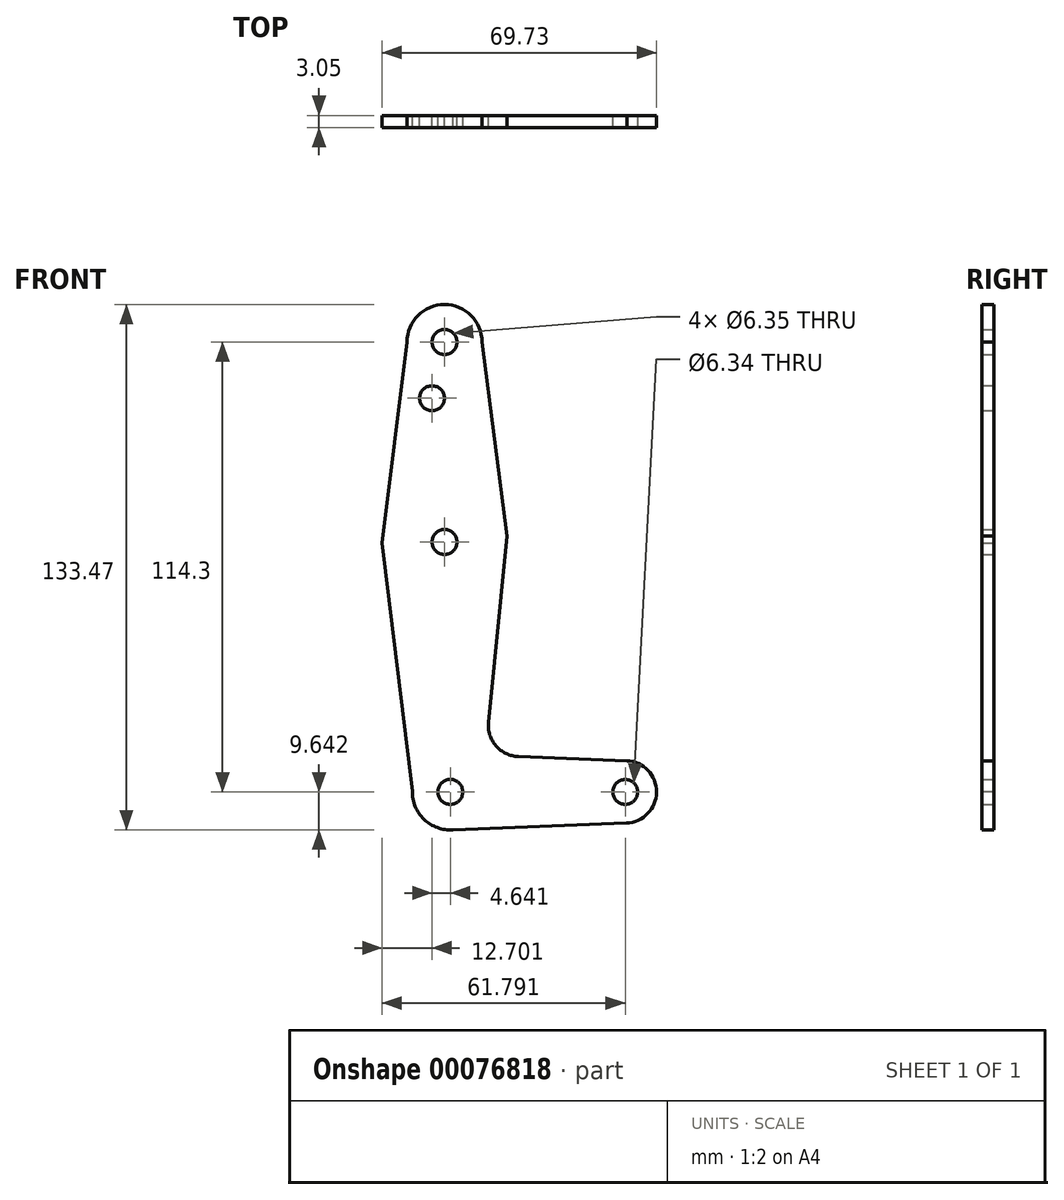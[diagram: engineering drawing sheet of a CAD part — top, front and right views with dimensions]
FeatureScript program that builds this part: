
annotation { "Feature Type Name" : "Feature", "Feature Type Description" : "" }
export const myFeature = defineFeature(function(context is Context, id is Id, definition is map)
    precondition{}
    {
        {
            var Q0;
            Q0=qCreatedBy(makeId("Front.planeOp"),FACE);
            var sketch = newSketch(context, id + "F0", { "sketchPlane" : qUnion([Q0])});
            skLineSegment(sketch, "E0", {"start": v(-40.14, -49.22) * mm, "end": v(4.31, -49.22) * mm});
            skCircle(sketch, "E1", {"center": v(-41.6, 65.08) * mm, "radius": 9.53 * mm});
            skCircle(sketch, "E2", {"center": v(-41.6, 14.28) * mm, "radius": 15.88 * mm});
            skCircle(sketch, "E3", {"center": v(-40.14, -49.22) * mm, "radius": 9.65 * mm});
            skCircle(sketch, "E4", {"center": v(4.31, -49.22) * mm, "radius": 7.94 * mm});
            skLineSegment(sketch, "E5", {"start": v(-41.6, 65.08) * mm, "end": v(-41.6, 14.28) * mm});
            skLineSegment(sketch, "E6", {"start": v(-41.6, 14.28) * mm, "end": v(-40.14, -49.22) * mm});
            skLineSegment(sketch, "E7", {"start": v(-32.08, 65.08) * mm, "end": v(-25.8, 15.75) * mm});
            skLineSegment(sketch, "E8", {"start": v(-25.8, 15.75) * mm, "end": v(-30.45, -31.5) * mm});
            skLineSegment(sketch, "E9", {"start": v(-49.78, -49.04) * mm, "end": v(-57.48, 14) * mm});
            skLineSegment(sketch, "E10", {"start": v(-51.13, 65.08) * mm, "end": v(-57.48, 14) * mm});
            skLineSegment(sketch, "E11", {"start": v(4.7, -41.29) * mm, "end": v(-22.85, -40.23) * mm});
            skLineSegment(sketch, "E12", {"start": v(-39.48, -58.84) * mm, "end": v(4.62, -57.15) * mm});
            skCircle(sketch, "E13", {"center": v(-41.6, 65.08) * mm, "radius": 3.18 * mm});
            skCircle(sketch, "E14", {"center": v(-41.6, 14.28) * mm, "radius": 3.18 * mm});
            skCircle(sketch, "E15", {"center": v(-40.14, -49.22) * mm, "radius": 3.18 * mm});
            skCircle(sketch, "E16", {"center": v(4.31, -49.22) * mm, "radius": 3.17 * mm});
            skArc(sketch, "E17.filletArc", {"start": v(-30.45, -31.5) * mm, "mid": v(-28.53, -37.51) * mm, "end": v(-22.85, -40.23) * mm});
            skCircle(sketch, "E18", {"center": v(-44.78, 50.8) * mm, "radius": 3.18 * mm});
            skSolve(sketch);
        }
        {
            var Q0;
            {var subQ0=sQuery(id+"F0.wireOp",EDGE,"E18");Q0=makeQuery(id+"F0.imprint","IMPRINT",FACE,{"disambiguationData":[TD([[makeQuery(id+"F0.imprint","IMPRINT",EDGE,{"derivedFrom":subQ0}),-1.0]])]});}
            var Q1;
            {var subQ4=sQuery(id+"F0.wireOp",EDGE,"E1");var subQ6=sQuery(id+"F0.wireOp",EDGE,"E7");var subQ8=makeQuery(id+"F0.imprint","INTERSECT",VERTEX,{"derivedFrom":[subQ4,subQ6]});Q1=makeQuery(id+"F0.imprint","IMPRINT",FACE,{"disambiguationData":[TD([[makeQuery(id+"F0.imprint","IMPRINT",EDGE,{"disambiguationData":[TD([[subQ8,1.0]])],"derivedFrom":subQ4}),-1.0]])]});}
            var Q2;
            Q2=makeQuery(id+"F0.imprint","IMPRINT",FACE,{"disambiguationData":[TD([[makeQuery(id+"F0.imprint","IMPRINT",EDGE,{"derivedFrom":sQuery(id+"F0.wireOp",EDGE,"E13")}),-1.0]])]});
            var Q3;
            {var subQ1=sQuery(id+"F0.wireOp",EDGE,"E2");var subQ8=sQuery(id+"F0.wireOp",EDGE,"E10");var subQ11=makeQuery(id+"F0.imprint","INTERSECT",VERTEX,{"derivedFrom":[subQ1,subQ8]});Q3=makeQuery(id+"F0.imprint","IMPRINT",FACE,{"disambiguationData":[TD([[makeQuery(id+"F0.imprint","IMPRINT",EDGE,{"disambiguationData":[TD([[subQ11,1.0]])],"derivedFrom":subQ1}),1.0]])]});}
            var Q4;
            {var subQ1=sQuery(id+"F0.wireOp",EDGE,"E2");var subQ10=sQuery(id+"F0.wireOp",EDGE,"E7");var subQ11=makeQuery(id+"F0.imprint","INTERSECT",VERTEX,{"derivedFrom":[subQ1,subQ10]});Q4=makeQuery(id+"F0.imprint","IMPRINT",FACE,{"disambiguationData":[TD([[makeQuery(id+"F0.imprint","IMPRINT",EDGE,{"disambiguationData":[TD([[subQ11,-1.0]])],"derivedFrom":subQ1}),1.0]])]});}
            var Q5;
            {var subQ5=sQuery(id+"F0.wireOp",EDGE,"E12");Q5=makeQuery(id+"F0.imprint","IMPRINT",FACE,{"disambiguationData":[TD([[makeQuery(id+"F0.imprint","IMPRINT",EDGE,{"derivedFrom":subQ5}),1.0]])]});}
            var Q6;
            {var subQ0=sQuery(id+"F0.wireOp",EDGE,"E9");var subQ1=sQuery(id+"F0.wireOp",EDGE,"E2");var subQ2=makeQuery(id+"F0.imprint","INTERSECT",VERTEX,{"derivedFrom":[subQ1,subQ0]});Q6=makeQuery(id+"F0.imprint","IMPRINT",FACE,{"disambiguationData":[TD([[makeQuery(id+"F0.imprint","IMPRINT",EDGE,{"disambiguationData":[TD([[subQ2,-1.0]])],"derivedFrom":subQ1}),-1.0]])]});}
            var Q7;
            {var subQ0=sQuery(id+"F0.wireOp",EDGE,"E15");var subQ1=sQuery(id+"F0.wireOp",EDGE,"E0");var subQ2=makeQuery(id+"F0.imprint","INTERSECT",VERTEX,{"derivedFrom":[subQ1,subQ0]});Q7=makeQuery(id+"F0.imprint","IMPRINT",FACE,{"disambiguationData":[TD([[makeQuery(id+"F0.imprint","IMPRINT",EDGE,{"disambiguationData":[TD([[subQ2,-1.0]])],"derivedFrom":subQ1}),1.0]])]});}
            var Q8;
            {var subQ5=sQuery(id+"F0.wireOp",EDGE,"E0");var subQ7=sQuery(id+"F0.wireOp",EDGE,"E15");var subQ8=makeQuery(id+"F0.imprint","INTERSECT",VERTEX,{"derivedFrom":[subQ5,subQ7]});Q8=makeQuery(id+"F0.imprint","IMPRINT",FACE,{"disambiguationData":[TD([[makeQuery(id+"F0.imprint","IMPRINT",EDGE,{"disambiguationData":[TD([[subQ8,-1.0]])],"derivedFrom":subQ5}),-1.0]])]});}
            var Q9;
            Q9=makeQuery(id+"F0.imprint","IMPRINT",FACE,{"disambiguationData":[TD([[makeQuery(id+"F0.imprint","IMPRINT",EDGE,{"derivedFrom":sQuery(id+"F0.wireOp",EDGE,"E16")}),-1.0]])]});
            var Q10;
            {var subQ13=sQuery(id+"F0.wireOp",EDGE,"E17.filletArc");Q10=makeQuery(id+"F0.imprint","IMPRINT",FACE,{"disambiguationData":[TD([[makeQuery(id+"F0.imprint","IMPRINT",EDGE,{"derivedFrom":subQ13}),-1.0]])]});}
            extrude(context, id + "F1", {"entities" : qUnion([Q0, Q1, Q2, Q3, Q4, Q5, Q6, Q7, Q8, Q9, Q10]), "depth" : 3.05 * mm});
        }
    });
